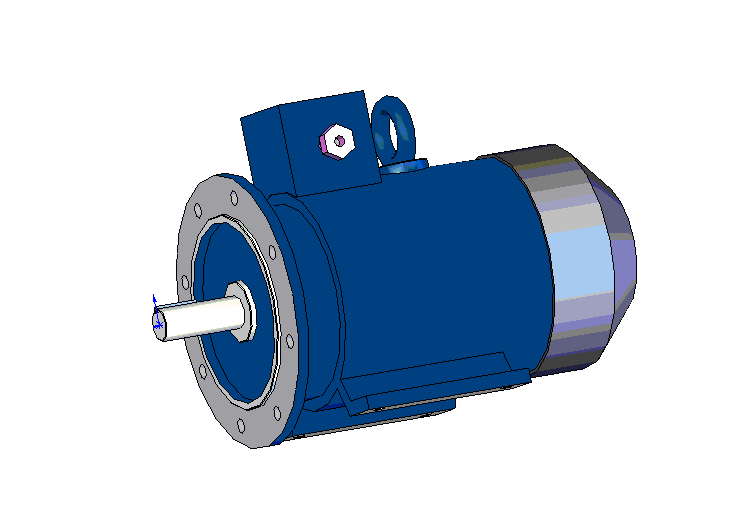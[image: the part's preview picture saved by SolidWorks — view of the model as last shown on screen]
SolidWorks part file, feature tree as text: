
SOLIDWORKS PART (.sldprt)
format: sldprt  version: not decoded by parser v0  size: 707,072 bytes
history: native  units: mm
features: sketch x18, extrude x12, plane x4, cut_extrude x4, chamfer x3, material x1, sweep x1 (+10 scaffold rows collapsed)
feature tree (53):
  scaffold x10  (default folders/planes/origin — collapsed)
  material  "Ст.3 ГОСТ 380-88"
  plane  "Спереди"
  plane  "Сверху"
  plane  "Справа"
  sketch  "Эскиз1"  dims[D1=42.0mm]
  extrude  "Вытянуть1"  Depth=110mm
  sketch  "Эскиз2"  dims[D1=8.0mm D2=8.0mm D3=45.0mm]
  extrude  "Вытянуть2"  Depth=55mm
  sketch  "Эскиз3"  dims[D1=350.0mm]
  extrude  "Вытянуть3"  Depth=15mm
  sketch  "Эскиз4"  dims[D1=250.0mm D2=232.0mm]
  extrude  "Вытянуть4"  Depth=5mm
  sketch  "Эскиз5"  dims[D1=232.0mm D2=80.0mm]
  cut_extrude  "Вырез-Вытянуть1"  Depth=8mm
  chamfer  "Фаска1"  Distance=1mm Angle=45deg
  sketch  "Эскиз6"  dims[c1.D2=19.0mm c1.D1=~222.342459mm c2.D1=22.5deg c2.D3=150.0mm c2.D4=150.0mm c2.D5=150.0mm]
  cut_extrude  "Вырез-Вытянуть2"  [1 undecoded]
  sketch  "Эскиз7"  dims[D1=250.0mm]
  extrude  "Вытянуть5"  Depth=68mm
  sketch  "Эскиз8"  dims[D1=280.0mm]
  extrude  "Вытянуть6"  Depth=292mm
  sketch  "Эскиз9"  dims[D1=288.0mm]
  extrude  "Вытянуть7"  Depth=145mm
  chamfer  "Фаска2"  Distance=60mm Angle=45deg
  sketch  "Эскиз10"  dims[c1.D1=18.0mm c1.D2=18.0mm c1.D3=~100.823354mm c2.D3=30.0deg c2.D4=50.0mm c2.D5=152.0mm c2.D6=160.0mm c2.D7=~105.04342mm]
  extrude  "Вытянуть8"  Depth=228mm
  sketch  "Эскиз11"  dims[D2=15.0mm D1=218.0mm D3=127.0mm D4=90.0deg D5=396.0mm D6=254.0mm D7=178.0mm]
  cut_extrude  "Вырез-Вытянуть3"  [1 undecoded]
  sketch  "Эскиз12"  dims[D1=120.0mm D2=120.0mm D3=1.0mm]
  extrude  "Вытянуть9"  Depth=245mm
  sketch  "Эскиз13"  dims[D1=70.0mm D2=370.0mm]
  extrude  "Вытянуть10"  Depth=150mm
  chamfer  "Фаска3"  Distance=1mm Angle=45deg
  plane  "Плоскость1"  Offset=370mm
  sketch  "Эскиз14"  dims[D1=76.0mm]
  sketch  "Эскиз15"  dims[D1=24.0mm D2=76.0mm]
  sweep  "По траектории1"
  sketch  "Эскиз16"  dims[D1=32.0mm D2=60.0mm D3=60.0mm]
  extrude  "Вытянуть11"  Depth=14mm
  sketch  "Эскиз17"  dims[D1=19.5mm]
  extrude  "Вытянуть12"  Depth=16mm
  sketch  "Эскиз18"  dims[D1=14.0mm]
  cut_extrude  "Вырез-Вытянуть4"  Depth=16mm
decode coverage: 35 of 38 modeling features carry decoded parameters
note: ~ marks probable driven/reference dimensions
note: 2 parameter values undecoded
note: suppression state not decoded; provenance and decode notes live in map.json
